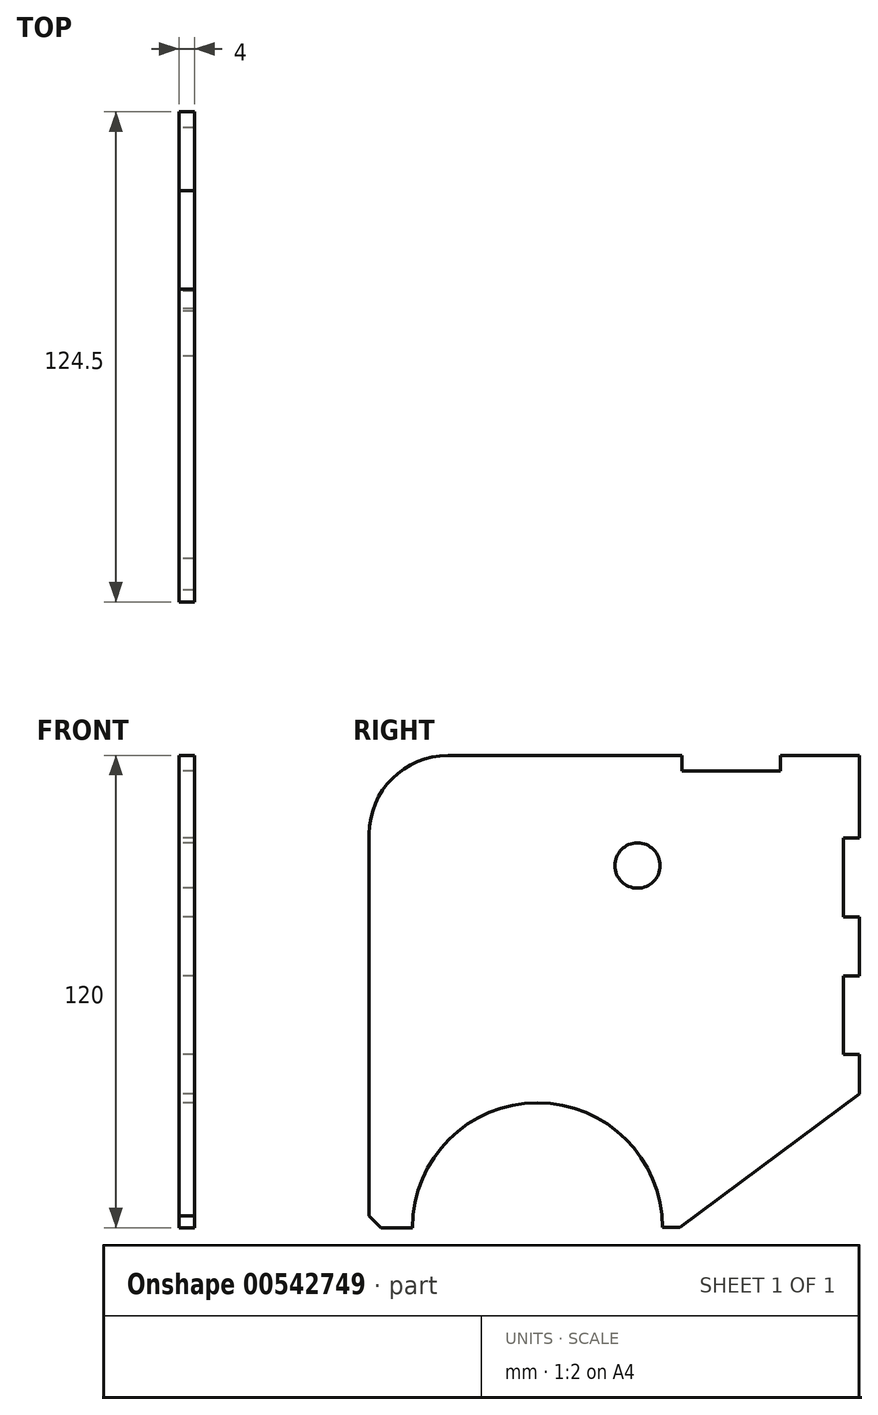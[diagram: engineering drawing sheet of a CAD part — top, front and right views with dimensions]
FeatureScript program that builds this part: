
annotation { "Feature Type Name" : "Feature", "Feature Type Description" : "" }
export const myFeature = defineFeature(function(context is Context, id is Id, definition is map)
    precondition{}
    {
        {
            var Q0;
            Q0=qCreatedBy(makeId("Right.planeOp"),FACE);
            var sketch = newSketch(context, id + "F0", { "sketchPlane" : qUnion([Q0])});
            skArc(sketch, "E0", {"start": v(2.7, -74.14) * mm, "mid": v(-29.05, -42.41) * mm, "end": v(-60.8, -74.16) * mm});
            skLineSegment(sketch, "E1", {"start": v(-60.8, -74.16) * mm, "end": v(-68.8, -74.16) * mm});
            skLineSegment(sketch, "E2", {"start": v(52.7, 45.84) * mm, "end": v(52.7, 24.84) * mm});
            skCircle(sketch, "E3", {"center": v(-3.64, 17.84) * mm, "radius": 5.75 * mm});
            skPoint(sketch, "E4.orphan", {"position": v(52.7, -75.1) * mm});
            skLineSegment(sketch, "E5", {"start": v(-71.8, -71.16) * mm, "end": v(-68.8, -74.16) * mm});
            skPoint(sketch, "E6.orphan", {"position": v(-71.8, 45.84) * mm});
            skLineSegment(sketch, "E7.top", {"start": v(7.7, 41.84) * mm, "end": v(32.7, 41.84) * mm});
            skLineSegment(sketch, "E7.left", {"start": v(7.7, 45.84) * mm, "end": v(7.7, 41.84) * mm});
            skLineSegment(sketch, "E7.right", {"start": v(32.7, 45.84) * mm, "end": v(32.7, 41.84) * mm});
            skLineSegment(sketch, "E8.trimOffspring", {"start": v(32.7, 45.84) * mm, "end": v(52.7, 45.84) * mm});
            skLineSegment(sketch, "E9.bottom", {"start": v(52.7, 24.84) * mm, "end": v(48.7, 24.84) * mm});
            skLineSegment(sketch, "E9.top", {"start": v(52.7, 4.84) * mm, "end": v(48.7, 4.84) * mm});
            skLineSegment(sketch, "E9.right", {"start": v(48.7, 24.84) * mm, "end": v(48.7, 4.84) * mm});
            skLineSegment(sketch, "E10.bottom", {"start": v(52.7, -10.16) * mm, "end": v(48.7, -10.16) * mm});
            skLineSegment(sketch, "E10.top", {"start": v(52.7, -30.16) * mm, "end": v(48.7, -30.16) * mm});
            skLineSegment(sketch, "E10.right", {"start": v(48.7, -10.16) * mm, "end": v(48.7, -30.16) * mm});
            skLineSegment(sketch, "E11", {"start": v(-71.8, 25.84) * mm, "end": v(-71.8, -71.16) * mm});
            skLineSegment(sketch, "E12.trimOffspring", {"start": v(52.7, -30.16) * mm, "end": v(52.7, -40.16) * mm});
            skLineSegment(sketch, "E13", {"start": v(52.7, 4.84) * mm, "end": v(52.7, -10.16) * mm});
            skLineSegment(sketch, "E14", {"start": v(-51.8, 45.84) * mm, "end": v(7.7, 45.84) * mm});
            skLineSegment(sketch, "E15", {"start": v(2.7, -74.14) * mm, "end": v(7.1, -74.14) * mm});
            skLineSegment(sketch, "E16", {"start": v(7.1, -74.14) * mm, "end": v(52.7, -40.16) * mm});
            skArc(sketch, "E17", {"start": v(-51.8, 45.84) * mm, "mid": v(-65.93, 39.98) * mm, "end": v(-71.8, 25.84) * mm});
            skSolve(sketch);
        }
        {
            var Q0;
            Q0=makeQuery(id+"F0.imprint","IMPRINT",FACE,{"disambiguationData":[TD([[makeQuery(id+"F0.imprint","IMPRINT",EDGE,{"derivedFrom":sQuery(id+"F0.wireOp",EDGE,"E0")}),-1.0]])]});
            extrude(context, id + "F1", {"entities" : qUnion([Q0]), "depth" : 4 * mm, "offsetDistance" : 25 * mm});
        }
    });
